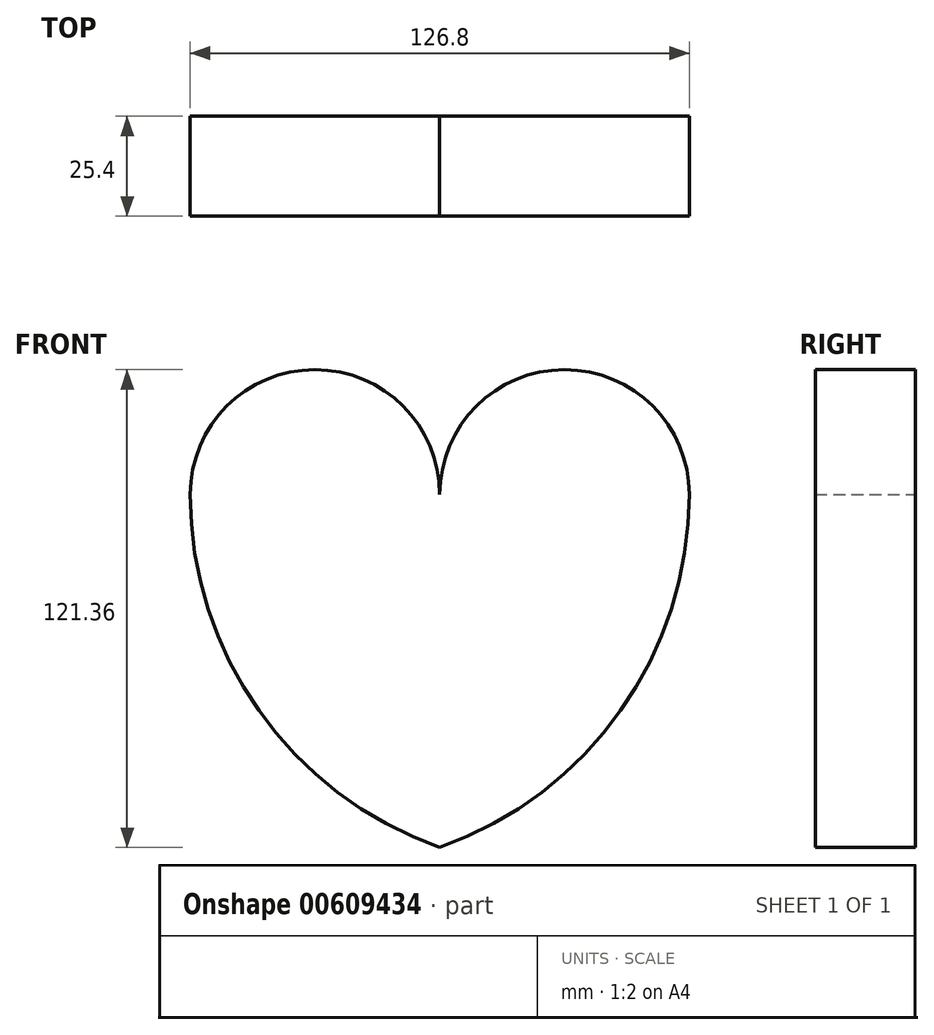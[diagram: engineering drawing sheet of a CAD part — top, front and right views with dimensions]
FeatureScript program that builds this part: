
annotation { "Feature Type Name" : "Feature", "Feature Type Description" : "" }
export const myFeature = defineFeature(function(context is Context, id is Id, definition is map)
    precondition{}
    {
        {
            var Q0;
            Q0=qCreatedBy(makeId("Front.planeOp"),FACE);
            var sketch = newSketch(context, id + "F0", { "sketchPlane" : qUnion([Q0])});
            skArc(sketch, "E0", {"start": v(0, 0) * mm, "mid": v(-31.7, 31.7) * mm, "end": v(-63.4, 0) * mm});
            skArc(sketch, "E1.MirrorC", {"start": v(0, 0) * mm, "mid": v(31.7, 31.7) * mm, "end": v(63.4, 0) * mm});
            skArc(sketch, "E2", {"start": v(63.4, 0) * mm, "mid": v(45.95, -54.9) * mm, "end": v(0, -89.66) * mm});
            skArc(sketch, "E3", {"start": v(-63.4, 0) * mm, "mid": v(-45.95, -54.9) * mm, "end": v(0, -89.66) * mm});
            skPoint(sketch, "E4.start.orphan", {"position": v(0, -73.34) * mm});
            skSolve(sketch);
        }
        {
            var Q0;
            Q0=makeQuery(id+"F0.imprint","IMPRINT",FACE,{"disambiguationData":[TD([[makeQuery(id+"F0.imprint","IMPRINT",EDGE,{"derivedFrom":sQuery(id+"F0.wireOp",EDGE,"E0")}),1.0]])]});
            extrude(context, id + "F1", {"entities" : qUnion([Q0]), "depth" : 25.4 * mm, "offsetDistance" : 25.4 * mm});
        }
    });
